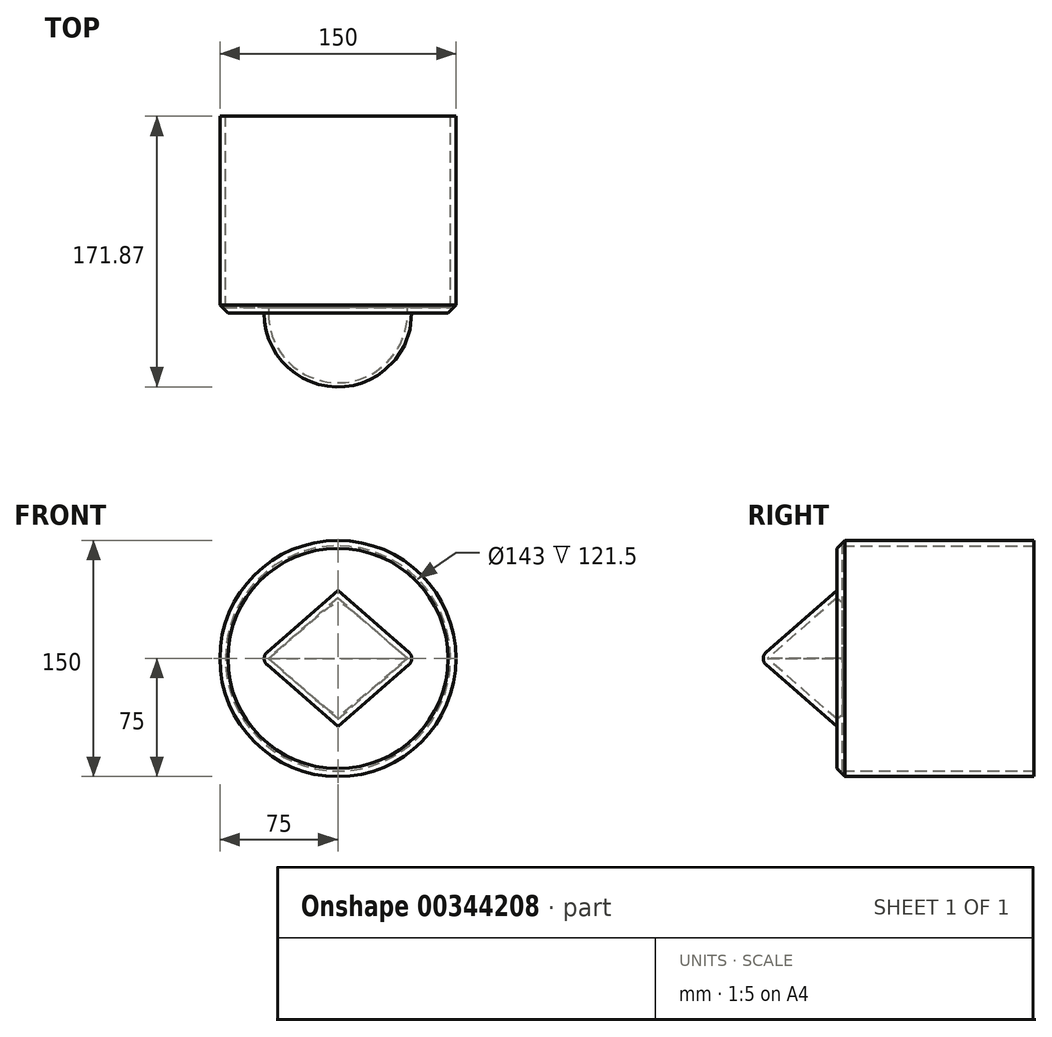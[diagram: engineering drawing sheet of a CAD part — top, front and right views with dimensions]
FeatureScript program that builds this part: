
annotation { "Feature Type Name" : "Feature", "Feature Type Description" : "" }
export const myFeature = defineFeature(function(context is Context, id is Id, definition is map)
    precondition{}
    {
        {
            var Q0;
            Q0=qCreatedBy(makeId("Front.planeOp"),FACE);
            var sketch = newSketch(context, id + "F0", { "sketchPlane" : qUnion([Q0])});
            skCircle(sketch, "E0", {"center": v(0, 0) * mm, "radius": 75 * mm});
            skSolve(sketch);
        }
        {
            var Q0;
            Q0=makeQuery(id+"F0.imprint","IMPRINT",FACE,{"disambiguationData":[TD([[makeQuery(id+"F0.imprint","IMPRINT",EDGE,{"derivedFrom":sQuery(id+"F0.wireOp",EDGE,"E0")}),1.0]])]});
            extrude(context, id + "F1", {"entities" : qUnion([Q0]), "depth" : 125 * mm});
        }
        {
            var Q0;
            Q0=makeQuery(id+"F1.opExtrude","CAP_FACE",FACE,{"disambiguationData":[OSD([sQuery(id+"F0.wireOp",EDGE,"E0")])],"isStart":false});
            var sketch = newSketch(context, id + "F2", { "sketchPlane" : qUnion([Q0])});
            skLineSegment(sketch, "E1", {"start": v(0, 0) * mm, "end": v(0, 43.16) * mm});
            skLineSegment(sketch, "E2", {"start": v(0, 43.16) * mm, "end": v(49.52, 0) * mm});
            skLineSegment(sketch, "E3", {"start": v(49.52, 0) * mm, "end": v(0, 0) * mm});
            skSolve(sketch);
        }
        {
            var Q0;
            Q0=makeQuery(id+"F2.imprint","IMPRINT",FACE,{"disambiguationData":[TD([[makeQuery(id+"F2.imprint","IMPRINT",EDGE,{"derivedFrom":sQuery(id+"F2.wireOp",EDGE,"E1")}),1.0]])]});
            var sketch = newSketch(context, id + "F3", { "sketchPlane" : qUnion([Q0])});
            skLineSegment(sketch, "E4", {"start": v(0, 83.1) * mm, "end": v(0, -144.44) * mm, "construction": true});
            skSolve(sketch);
        }
        {
            var Q0;
            Q0=makeQuery(id+"F2.imprint","IMPRINT",FACE,{"disambiguationData":[TD([[makeQuery(id+"F2.imprint","IMPRINT",EDGE,{"derivedFrom":sQuery(id+"F2.wireOp",EDGE,"E1")}),-1.0]])]});
            var Q1;
            Q1=sQuery(id+"F3.wireOp",EDGE,"E4");
            revolve(context, id + "F4", {"operationType" : NewBodyOperationType.ADD, "entities" : qUnion([Q0]), "axis" : qUnion([Q1]), "revolveType" : RevolveType.FULL});
        }
        {
            var Q0;
            Q0=makeQuery(id+"F1.opExtrude","SWEPT_BODY",BODY,{"disambiguationData":[OSD([sQuery(id+"F0.wireOp",EDGE,"E0")])]});
            var Q1;
            Q1=qCreatedBy(makeId("Top.planeOp"),FACE);
            mirror(context, id + "F5", {"operationType" : NewBodyOperationType.ADD, "entities" : qUnion([Q0]), "mirrorPlane" : qUnion([Q1])});
        }
        {
            var Q0;
            Q0=makeQuery(id+"F1.opExtrude","CAP_FACE",FACE,{"disambiguationData":[OSD([sQuery(id+"F0.wireOp",EDGE,"E0")])],"isStart":true});
            shell(context, id + "F6", {"entities" : qUnion([Q0]), "thickness" : 3.5 * mm});
        }
        {
            var Q0;
            Q0=makeQuery(id+"F1.opExtrude","CAP_EDGE",EDGE,{"disambiguationData":[OSD([sQuery(id+"F0.wireOp",EDGE,"E0")])],"isStart":false});
            chamfer(context, id + "F7", {"entities" : qUnion([Q0]), "width" : 5.08 * mm, "tangentPropagation" : true});
        }
        {
            var Q0;
            {var subQ0=makeQuery(id+"F4.opRevolve","SWEPT_EDGE",EDGE,{"disambiguationData":[OSD([sQuery(id+"F2.wireOp",EDGE,"E2"),sQuery(id+"F2.wireOp",EDGE,"E3")])]});Q0=makeQuery(id+"F5.boolean.opBoolean","MERGE",EDGE,{"derivedFrom":[subQ0,makeQuery(id+"F5.opPattern","COPY",EDGE,{"derivedFrom":subQ0,"instanceName":"1"})]});}
            fillet(context, id + "F8", {"entities" : qUnion([Q0]), "radius" : 5.08 * mm, "tangentPropagation" : true, "allowEdgeOverflow" : false});
        }
    });
